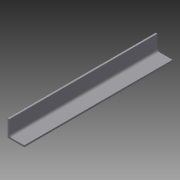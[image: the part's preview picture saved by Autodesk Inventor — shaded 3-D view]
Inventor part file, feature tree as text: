
AUTODESK INVENTOR PART (.ipt)
format: ipt  version: 2014 (Build 180170000, 170)  size: 94,720 bytes
history: native  units: in
note: dims shown in document units (in); Inventor stores cm internally (conversion verified against a paired STEP export)
features: extrude x3, sketch x3
ambient origin geometry x8: Origin, YZ Plane, XZ Plane, XY Plane, X Axis, Y Axis, Z Axis, Center Point
bodies: Solid1 (feature_tree)
feature tree (6):
  extrude  "Extrusion1"  Depth=1.0in
  extrude  "Extrusion4"  Depth=0.125in
  extrude  "Extrusion5"  Depth=1.0in
  sketch  "Sketch1"  dims[d0=1.0in d1=1.0in]
  sketch  "Sketch4"  dims[d2=0.1in d3=0.125in]
  sketch  "Sketch5"  dims[d4=8.8583in d5=0.0in d19=2.0in d20=0.25in d21=0.15in d22=2.5in d25=1.0in d26=0.0in d27=0.0591in d28=0.0in]
